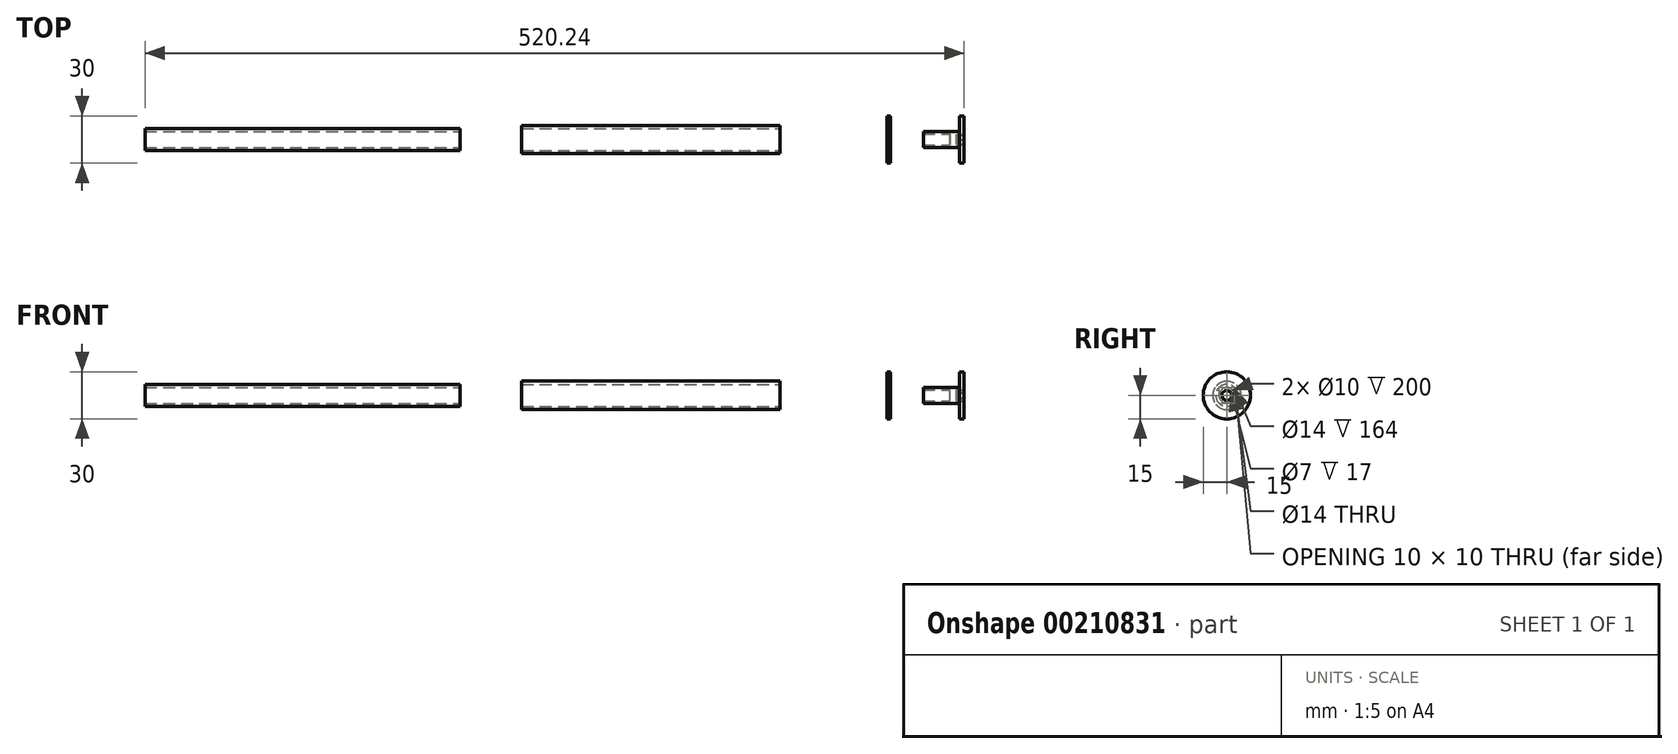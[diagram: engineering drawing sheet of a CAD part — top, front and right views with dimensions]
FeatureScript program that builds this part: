
annotation { "Feature Type Name" : "Feature", "Feature Type Description" : "" }
export const myFeature = defineFeature(function(context is Context, id is Id, definition is map)
    precondition{}
    {
        {
            var Q0;
            Q0=qCreatedBy(makeId("Front.planeOp"),FACE);
            var sketch = newSketch(context, id + "F0", { "sketchPlane" : qUnion([Q0])});
            skLineSegment(sketch, "E0", {"start": v(213.44, 0) * mm, "end": v(164.54, 0) * mm, "construction": true});
            skLineSegment(sketch, "E1.bottom", {"start": v(-106.8, -7.5) * mm, "end": v(-306.8, -7.5) * mm});
            skLineSegment(sketch, "E1.top", {"start": v(-106.8, 7.5) * mm, "end": v(-306.8, 7.5) * mm});
            skLineSegment(sketch, "E1.left", {"start": v(-106.8, -7.5) * mm, "end": v(-106.8, 7.5) * mm});
            skLineSegment(sketch, "E1.right", {"start": v(-306.8, -7.5) * mm, "end": v(-306.8, 7.5) * mm});
            skPoint(sketch, "E1.middle", {"position": v(-206.8, 0) * mm});
            skLineSegment(sketch, "E2", {"start": v(-67.65, 0) * mm, "end": v(-384.55, 0) * mm, "construction": true});
            skLineSegment(sketch, "E3", {"start": v(96.35, 0) * mm, "end": v(-67.65, 0) * mm, "construction": true});
            skLineSegment(sketch, "E4", {"start": v(164.54, 0) * mm, "end": v(96.35, 0) * mm, "construction": true});
            skSolve(sketch);
        }
        {
            var Q0;
            Q0=sQuery(id+"F0.wireOp",VERTEX,"E1.left.end");
            var Q1;
            Q1=qCreatedBy(makeId("Right.planeOp"),FACE);
            cPlane(context, id + "F1", {"entities" : qUnion([Q0, Q1]), "cplaneType" : CPlaneType.PLANE_POINT, "offset" : 25 * mm, "width" : 150 * mm, "height" : 150 * mm});
        }
        {
            var Q0;
            Q0=qCreatedBy(id+"F1.planeOp",FACE);
            var sketch = newSketch(context, id + "F2", { "sketchPlane" : qUnion([Q0])});
            skCircle(sketch, "E5", {"center": v(0, 0) * mm, "radius": 7 * mm});
            skCircle(sketch, "E6.0", {"center": v(0, 0) * mm, "radius": 5 * mm});
            skSolve(sketch);
        }
        {
            var Q0;
            Q0=makeQuery(id+"F2.imprint","IMPRINT",FACE,{"disambiguationData":[TD([[makeQuery(id+"F2.imprint","IMPRINT",EDGE,{"derivedFrom":sQuery(id+"F2.wireOp",EDGE,"E5")}),1.0]])]});
            var Q1;
            Q1=sQuery(id+"F0.wireOp",VERTEX,"E1.right.end");
            extrude(context, id + "F3", {"entities" : qUnion([Q0]), "endBound" : BoundingType.UP_TO_VERTEX, "oppositeDirection" : true, "endBoundEntityVertex" : qUnion([Q1]), "depth" : 25 * mm});
        }
        {
            var Q0;
            Q0=qCreatedBy(makeId("Right.planeOp"),FACE);
            var Q1;
            Q1=sQuery(id+"F0.wireOp",VERTEX,"E3.start");
            cPlane(context, id + "F4", {"entities" : qUnion([Q0, Q1]), "cplaneType" : CPlaneType.PLANE_POINT, "offset" : 25 * mm, "width" : 150 * mm, "height" : 150 * mm});
        }
        {
            var Q0;
            Q0=sQuery(id+"F0.wireOp",VERTEX,"E0.end");
            var Q1;
            Q1=qCreatedBy(makeId("Right.planeOp"),FACE);
            cPlane(context, id + "F5", {"entities" : qUnion([Q0, Q1]), "cplaneType" : CPlaneType.PLANE_POINT, "offset" : 25 * mm, "width" : 150 * mm, "height" : 150 * mm});
        }
        {
            var Q0;
            Q0=sQuery(id+"F0.wireOp",VERTEX,"E0.start");
            var Q1;
            Q1=qCreatedBy(makeId("Right.planeOp"),FACE);
            cPlane(context, id + "F6", {"entities" : qUnion([Q0, Q1]), "cplaneType" : CPlaneType.PLANE_POINT, "offset" : 25 * mm, "width" : 150 * mm, "height" : 150 * mm});
        }
        {
            var Q0;
            Q0=qCreatedBy(id+"F4.planeOp",FACE);
            var sketch = newSketch(context, id + "F7", { "sketchPlane" : qUnion([Q0])});
            skCircle(sketch, "E7", {"center": v(0, 0) * mm, "radius": 7 * mm});
            skCircle(sketch, "E8", {"center": v(0, 0) * mm, "radius": 9 * mm});
            skSolve(sketch);
        }
        {
            var Q0;
            Q0=qCreatedBy(id+"F6.planeOp",FACE);
            var sketch = newSketch(context, id + "F8", { "sketchPlane" : qUnion([Q0])});
            skCircle(sketch, "E9", {"center": v(0, 0) * mm, "radius": 3.5 * mm});
            skCircle(sketch, "E10", {"center": v(0, 0) * mm, "radius": 5 * mm});
            skCircle(sketch, "E11", {"center": v(0, 0) * mm, "radius": 15 * mm});
            skCircle(sketch, "E12.cCircle", {"center": v(0, 0) * mm, "radius": 3 * mm, "construction": true});
            skLineSegment(sketch, "E12.0", {"start": v(3.07, -1.6) * mm, "end": v(0.15, -3.46) * mm});
            skLineSegment(sketch, "E12.1", {"start": v(0.15, -3.46) * mm, "end": v(-2.92, -1.86) * mm});
            skLineSegment(sketch, "E12.2", {"start": v(-2.92, -1.86) * mm, "end": v(-3.07, 1.6) * mm});
            skLineSegment(sketch, "E12.3", {"start": v(-3.07, 1.6) * mm, "end": v(-0.15, 3.46) * mm});
            skLineSegment(sketch, "E12.4", {"start": v(-0.15, 3.46) * mm, "end": v(2.92, 1.86) * mm});
            skLineSegment(sketch, "E12.5", {"start": v(2.92, 1.86) * mm, "end": v(3.07, -1.6) * mm});
            skPoint(sketch, "E12.0.midPoint", {"position": v(1.61, -2.53) * mm});
            skSolve(sketch);
        }
        {
            var Q0;
            Q0=makeQuery(id+"F2.imprint","IMPRINT",FACE,{"disambiguationData":[TD([[makeQuery(id+"F2.imprint","IMPRINT",EDGE,{"derivedFrom":sQuery(id+"F2.wireOp",EDGE,"E5")}),1.0]])]});
            var Q1;
            Q1=sQuery(id+"F0.wireOp",VERTEX,"E1.right.end");
            extrude(context, id + "F9", {"entities" : qUnion([Q0]), "endBound" : BoundingType.UP_TO_VERTEX, "oppositeDirection" : true, "endBoundEntityVertex" : qUnion([Q1]), "depth" : 25 * mm});
        }
        {
            var Q0;
            Q0=makeQuery(id+"F7.imprint","IMPRINT",FACE,{"disambiguationData":[TD([[makeQuery(id+"F7.imprint","IMPRINT",EDGE,{"derivedFrom":sQuery(id+"F7.wireOp",EDGE,"E7")}),-1.0]])]});
            var Q1;
            Q1=sQuery(id+"F0.wireOp",VERTEX,"E2.start");
            extrude(context, id + "F10", {"entities" : qUnion([Q0]), "endBound" : BoundingType.UP_TO_VERTEX, "oppositeDirection" : true, "endBoundEntityVertex" : qUnion([Q1]), "depth" : 25 * mm});
        }
        {
            var Q0;
            Q0=makeQuery(id+"F8.imprint","IMPRINT",FACE,{"disambiguationData":[TD([[makeQuery(id+"F8.imprint","IMPRINT",EDGE,{"derivedFrom":sQuery(id+"F8.wireOp",EDGE,"E9")}),-1.0]])]});
            extrude(context, id + "F11", {"entities" : qUnion([Q0]), "oppositeDirection" : true, "depth" : 26 * mm});
        }
        {
            var Q0;
            Q0=makeQuery(id+"F8.imprint","IMPRINT",FACE,{"disambiguationData":[TD([[makeQuery(id+"F8.imprint","IMPRINT",EDGE,{"derivedFrom":sQuery(id+"F8.wireOp",EDGE,"E10")}),-1.0]])]});
            extrude(context, id + "F12", {"entities" : qUnion([Q0]), "operationType" : NewBodyOperationType.ADD, "oppositeDirection" : true, "depth" : 3 * mm});
        }
        {
            var Q0;
            Q0=makeQuery(id+"F8.imprint","IMPRINT",FACE,{"disambiguationData":[TD([[makeQuery(id+"F8.imprint","IMPRINT",EDGE,{"derivedFrom":sQuery(id+"F8.wireOp",EDGE,"E9")}),1.0]])]});
            var Q1;
            Q1=makeQuery(id+"F8.imprint","IMPRINT",FACE,{"disambiguationData":[TD([[makeQuery(id+"F8.imprint","IMPRINT",EDGE,{"derivedFrom":sQuery(id+"F8.wireOp",EDGE,"E12.0")}),-1.0]])]});
            var Q2;
            Q2=sQuery(id+"F8.wireOp",EDGE,"E9");
            extrude(context, id + "F13", {"entities" : qUnion([Q0, Q1]), "operationType" : NewBodyOperationType.ADD, "surfaceEntities" : qUnion([Q2]), "oppositeDirection" : true, "depth" : 9 * mm});
        }
        {
            var Q0;
            Q0=makeQuery(id+"F8.imprint","IMPRINT",FACE,{"disambiguationData":[TD([[makeQuery(id+"F8.imprint","IMPRINT",EDGE,{"derivedFrom":sQuery(id+"F8.wireOp",EDGE,"E12.0")}),-1.0]])]});
            extrude(context, id + "F14", {"entities" : qUnion([Q0]), "operationType" : NewBodyOperationType.REMOVE, "oppositeDirection" : true, "depth" : 5 * mm});
        }
        {
            var Q0;
            Q0=qCreatedBy(id+"F5.planeOp",FACE);
            var sketch = newSketch(context, id + "F15", { "sketchPlane" : qUnion([Q0])});
            skCircle(sketch, "E13", {"center": v(0, 0) * mm, "radius": 15 * mm});
            skCircle(sketch, "E14", {"center": v(0, 0) * mm, "radius": 7 * mm});
            skSolve(sketch);
        }
        {
            var Q0;
            Q0=makeQuery(id+"F15.imprint","IMPRINT",FACE,{"disambiguationData":[TD([[makeQuery(id+"F15.imprint","IMPRINT",EDGE,{"derivedFrom":sQuery(id+"F15.wireOp",EDGE,"E13")}),1.0]])]});
            extrude(context, id + "F16", {"entities" : qUnion([Q0]), "depth" : 2 * mm});
        }
    });
